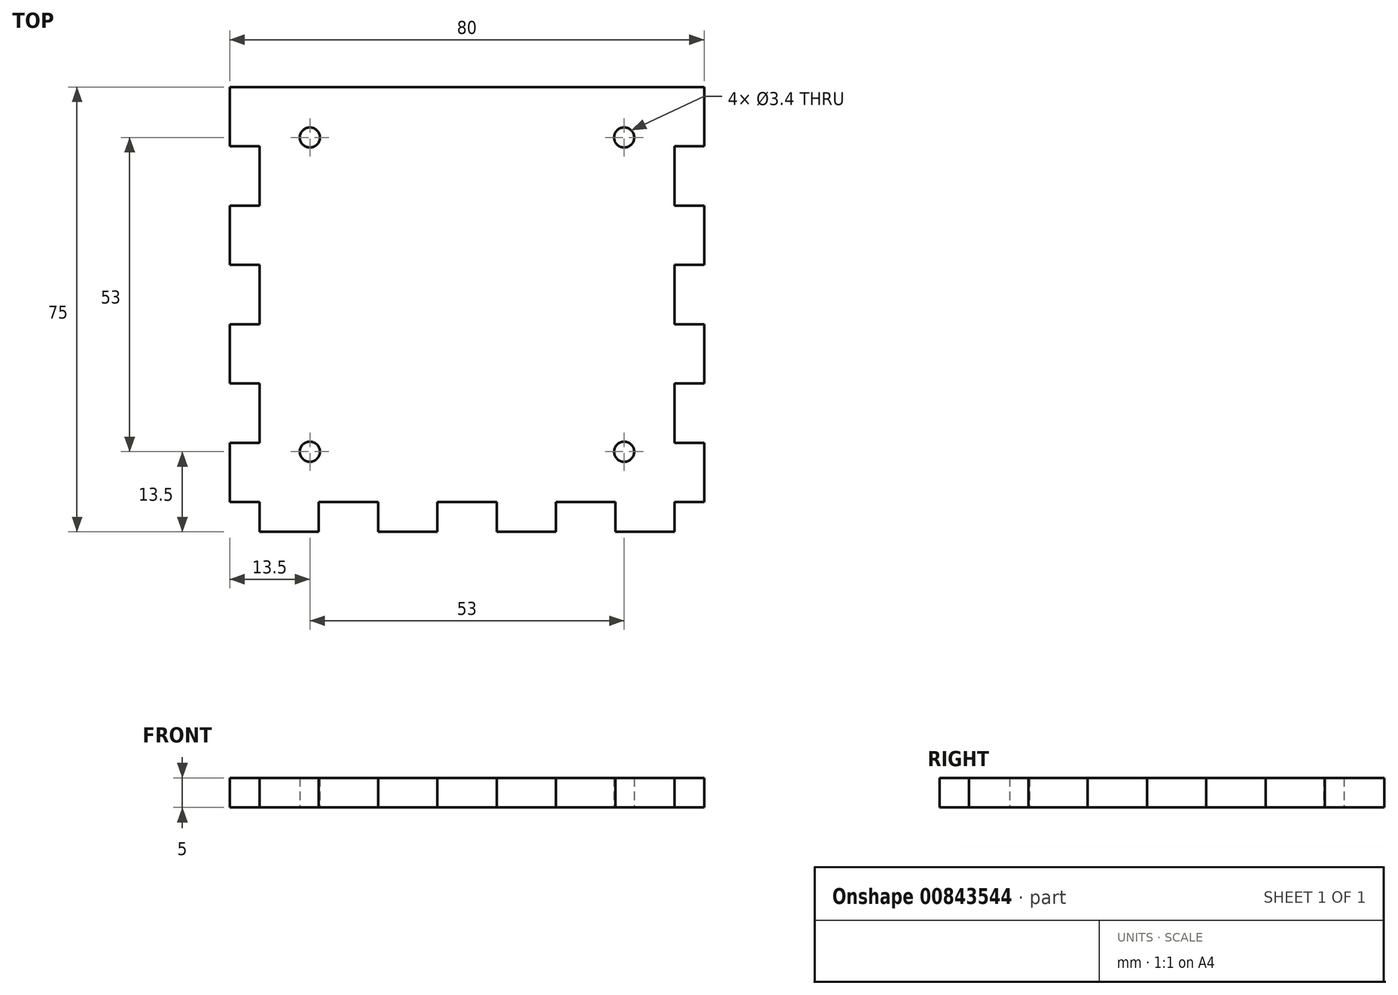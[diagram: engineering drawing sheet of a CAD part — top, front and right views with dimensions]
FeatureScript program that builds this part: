
annotation { "Feature Type Name" : "Feature", "Feature Type Description" : "" }
export const myFeature = defineFeature(function(context is Context, id is Id, definition is map)
    precondition{}
    {
        {
            var Q0;
            Q0=qCreatedBy(makeId("Top.planeOp"),FACE);
            var sketch = newSketch(context, id + "F0", { "sketchPlane" : qUnion([Q0])});
            skLineSegment(sketch, "E0.bottom", {"start": v(35, 35) * mm, "end": v(-35, 35) * mm});
            skLineSegment(sketch, "E0.top", {"start": v(35, -35) * mm, "end": v(-35, -35) * mm});
            skLineSegment(sketch, "E0.left", {"start": v(35, 35) * mm, "end": v(35, -35) * mm});
            skLineSegment(sketch, "E0.right", {"start": v(-35, 35) * mm, "end": v(-35, -35) * mm});
            skPoint(sketch, "E0.middle", {"position": v(0, 0) * mm});
            skSolve(sketch);
        }
        {
            var Q0;
            Q0=makeQuery(id+"F0.imprint","IMPRINT",FACE,{"disambiguationData":[TD([[makeQuery(id+"F0.imprint","IMPRINT",EDGE,{"derivedFrom":sQuery(id+"F0.wireOp",EDGE,"E0.bottom")}),1.0]])]});
            extrude(context, id + "F1", {"entities" : qUnion([Q0]), "endBound" : BoundingType.SYMMETRIC, "depth" : 5 * mm, "offsetDistance" : 25 * mm});
        }
        {
            var Q0;
            Q0=makeQuery(id+"F1.opExtrude","CAP_FACE",FACE,{"disambiguationData":[OSD([sQuery(id+"F0.wireOp",EDGE,"E0.bottom"),sQuery(id+"F0.wireOp",EDGE,"E0.top"),sQuery(id+"F0.wireOp",EDGE,"E0.left"),sQuery(id+"F0.wireOp",EDGE,"E0.right")])],"isStart":true});
            var sketch = newSketch(context, id + "F2", { "sketchPlane" : qUnion([Q0])});
            skLineSegment(sketch, "E1.bottom", {"start": v(-35, -35) * mm, "end": v(-40, -35) * mm});
            skLineSegment(sketch, "E1.top", {"start": v(-35, -25) * mm, "end": v(-40, -25) * mm});
            skLineSegment(sketch, "E1.left", {"start": v(-35, -35) * mm, "end": v(-35, -25) * mm});
            skLineSegment(sketch, "E1.right", {"start": v(-40, -35) * mm, "end": v(-40, -25) * mm});
            skLineSegment(sketch, "E2.bottom", {"start": v(35, -35) * mm, "end": v(40, -35) * mm});
            skLineSegment(sketch, "E2.top", {"start": v(35, -25) * mm, "end": v(40, -25) * mm});
            skLineSegment(sketch, "E2.left", {"start": v(35, -35) * mm, "end": v(35, -25) * mm});
            skLineSegment(sketch, "E2.right", {"start": v(40, -35) * mm, "end": v(40, -25) * mm});
            skLineSegment(sketch, "E3.0.1.0", {"start": v(35, -15) * mm, "end": v(40, -15) * mm});
            skLineSegment(sketch, "E3.0.1.1", {"start": v(40, -15) * mm, "end": v(40, -5) * mm});
            skLineSegment(sketch, "E3.0.1.2", {"start": v(-35, -15) * mm, "end": v(-35, -5) * mm});
            skLineSegment(sketch, "E3.0.1.3", {"start": v(-35, -15) * mm, "end": v(-40, -15) * mm});
            skLineSegment(sketch, "E3.0.1.4", {"start": v(35, -15) * mm, "end": v(35, -5) * mm});
            skLineSegment(sketch, "E3.0.1.5", {"start": v(-35, -5) * mm, "end": v(-40, -5) * mm});
            skLineSegment(sketch, "E3.0.1.6", {"start": v(35, -5) * mm, "end": v(40, -5) * mm});
            skLineSegment(sketch, "E3.0.1.7", {"start": v(-40, -15) * mm, "end": v(-40, -5) * mm});
            skLineSegment(sketch, "E3.0.2.0", {"start": v(35, 5) * mm, "end": v(40, 5) * mm});
            skLineSegment(sketch, "E3.0.2.1", {"start": v(40, 5) * mm, "end": v(40, 15) * mm});
            skLineSegment(sketch, "E3.0.2.2", {"start": v(-35, 5) * mm, "end": v(-35, 15) * mm});
            skLineSegment(sketch, "E3.0.2.3", {"start": v(-35, 5) * mm, "end": v(-40, 5) * mm});
            skLineSegment(sketch, "E3.0.2.4", {"start": v(35, 5) * mm, "end": v(35, 15) * mm});
            skLineSegment(sketch, "E3.0.2.5", {"start": v(-35, 15) * mm, "end": v(-40, 15) * mm});
            skLineSegment(sketch, "E3.0.2.6", {"start": v(35, 15) * mm, "end": v(40, 15) * mm});
            skLineSegment(sketch, "E3.0.2.7", {"start": v(-40, 5) * mm, "end": v(-40, 15) * mm});
            skLineSegment(sketch, "E3.direction1", {"start": v(-40, -35) * mm, "end": v(-15, -35) * mm, "construction": true});
            skLineSegment(sketch, "E3.direction2", {"start": v(-40, -35) * mm, "end": v(-40, -15) * mm, "construction": true});
            skLineSegment(sketch, "E4.0.0.3", {"start": v(35, 25) * mm, "end": v(40, 25) * mm});
            skLineSegment(sketch, "E4.3.0.3", {"start": v(40, 25) * mm, "end": v(40, 35) * mm});
            skLineSegment(sketch, "E4.6.0.3", {"start": v(-35, 25) * mm, "end": v(-35, 35) * mm});
            skLineSegment(sketch, "E4.9.0.3", {"start": v(-35, 25) * mm, "end": v(-40, 25) * mm});
            skLineSegment(sketch, "E4.12.0.3", {"start": v(35, 25) * mm, "end": v(35, 35) * mm});
            skLineSegment(sketch, "E4.15.0.3", {"start": v(-35, 35) * mm, "end": v(-40, 35) * mm});
            skLineSegment(sketch, "E4.18.0.3", {"start": v(35, 35) * mm, "end": v(40, 35) * mm});
            skLineSegment(sketch, "E4.21.0.3", {"start": v(-40, 25) * mm, "end": v(-40, 35) * mm});
            skSolve(sketch);
        }
        {
            var Q0;
            Q0 = qSketchRegion(id + "F2", true);
            var Q1;
            Q1=makeQuery(id+"F1.opExtrude","CAP_FACE",FACE,{"disambiguationData":[OSD([sQuery(id+"F0.wireOp",EDGE,"E0.bottom"),sQuery(id+"F0.wireOp",EDGE,"E0.top"),sQuery(id+"F0.wireOp",EDGE,"E0.left"),sQuery(id+"F0.wireOp",EDGE,"E0.right")])],"isStart":false});
            extrude(context, id + "F3", {"entities" : qUnion([Q0]), "operationType" : NewBodyOperationType.ADD, "endBound" : BoundingType.UP_TO_SURFACE, "oppositeDirection" : true, "depth" : 25 * mm, "endBoundEntityFace" : qUnion([Q1]), "offsetDistance" : 25 * mm});
        }
        {
            var Q0;
            Q0=makeQuery(id+"F3.boolean.opBoolean","MERGE",FACE,{"derivedFrom":[makeQuery(id+"F1.opExtrude","CAP_FACE",FACE,{"disambiguationData":[OSD([sQuery(id+"F0.wireOp",EDGE,"E0.bottom"),sQuery(id+"F0.wireOp",EDGE,"E0.top"),sQuery(id+"F0.wireOp",EDGE,"E0.left"),sQuery(id+"F0.wireOp",EDGE,"E0.right")])],"isStart":true}),makeQuery(id+"F3.opExtrude","CAP_FACE",FACE,{"disambiguationData":[OSD([sQuery(id+"F2.wireOp",EDGE,"E1.bottom"),sQuery(id+"F2.wireOp",EDGE,"E1.top"),sQuery(id+"F2.wireOp",EDGE,"E1.left"),sQuery(id+"F2.wireOp",EDGE,"E1.right")])],"isStart":true}),makeQuery(id+"F3.opExtrude","CAP_FACE",FACE,{"disambiguationData":[OSD([sQuery(id+"F2.wireOp",EDGE,"E2.bottom"),sQuery(id+"F2.wireOp",EDGE,"E2.top"),sQuery(id+"F2.wireOp",EDGE,"E2.left"),sQuery(id+"F2.wireOp",EDGE,"E2.right")])],"isStart":true}),makeQuery(id+"F3.opExtrude","CAP_FACE",FACE,{"disambiguationData":[OSD([sQuery(id+"F2.wireOp",EDGE,"E3.0.1.0"),sQuery(id+"F2.wireOp",EDGE,"E3.0.1.1"),sQuery(id+"F2.wireOp",EDGE,"E3.0.1.4"),sQuery(id+"F2.wireOp",EDGE,"E3.0.1.6")])],"isStart":true}),makeQuery(id+"F3.opExtrude","CAP_FACE",FACE,{"disambiguationData":[OSD([sQuery(id+"F2.wireOp",EDGE,"E3.0.1.2"),sQuery(id+"F2.wireOp",EDGE,"E3.0.1.3"),sQuery(id+"F2.wireOp",EDGE,"E3.0.1.5"),sQuery(id+"F2.wireOp",EDGE,"E3.0.1.7")])],"isStart":true}),makeQuery(id+"F3.opExtrude","CAP_FACE",FACE,{"disambiguationData":[OSD([sQuery(id+"F2.wireOp",EDGE,"E3.0.2.0"),sQuery(id+"F2.wireOp",EDGE,"E3.0.2.1"),sQuery(id+"F2.wireOp",EDGE,"E3.0.2.4"),sQuery(id+"F2.wireOp",EDGE,"E3.0.2.6")])],"isStart":true}),makeQuery(id+"F3.opExtrude","CAP_FACE",FACE,{"disambiguationData":[OSD([sQuery(id+"F2.wireOp",EDGE,"E3.0.2.2"),sQuery(id+"F2.wireOp",EDGE,"E3.0.2.3"),sQuery(id+"F2.wireOp",EDGE,"E3.0.2.5"),sQuery(id+"F2.wireOp",EDGE,"E3.0.2.7")])],"isStart":true}),makeQuery(id+"F3.opExtrude","CAP_FACE",FACE,{"disambiguationData":[OSD([sQuery(id+"F2.wireOp",EDGE,"E4.0.0.3"),sQuery(id+"F2.wireOp",EDGE,"E4.3.0.3"),sQuery(id+"F2.wireOp",EDGE,"E4.12.0.3"),sQuery(id+"F2.wireOp",EDGE,"E4.18.0.3")])],"isStart":true}),makeQuery(id+"F3.opExtrude","CAP_FACE",FACE,{"disambiguationData":[OSD([sQuery(id+"F2.wireOp",EDGE,"E4.6.0.3"),sQuery(id+"F2.wireOp",EDGE,"E4.9.0.3"),sQuery(id+"F2.wireOp",EDGE,"E4.15.0.3"),sQuery(id+"F2.wireOp",EDGE,"E4.21.0.3")])],"isStart":true})]});
            var sketch = newSketch(context, id + "F4", { "sketchPlane" : qUnion([Q0])});
            skLineSegment(sketch, "E5.bottom", {"start": v(-35, 35) * mm, "end": v(-25, 35) * mm});
            skLineSegment(sketch, "E5.top", {"start": v(-35, 40) * mm, "end": v(-25, 40) * mm});
            skLineSegment(sketch, "E5.left", {"start": v(-35, 35) * mm, "end": v(-35, 40) * mm});
            skLineSegment(sketch, "E5.right", {"start": v(-25, 35) * mm, "end": v(-25, 40) * mm});
            skLineSegment(sketch, "E6.1.0.0", {"start": v(-5, 35) * mm, "end": v(-5, 40) * mm});
            skLineSegment(sketch, "E6.1.0.1", {"start": v(-15, 40) * mm, "end": v(-5, 40) * mm});
            skLineSegment(sketch, "E6.1.0.2", {"start": v(-15, 35) * mm, "end": v(-15, 40) * mm});
            skLineSegment(sketch, "E6.1.0.3", {"start": v(-15, 35) * mm, "end": v(-5, 35) * mm});
            skLineSegment(sketch, "E6.2.0.0", {"start": v(15, 35) * mm, "end": v(15, 40) * mm});
            skLineSegment(sketch, "E6.2.0.1", {"start": v(5, 40) * mm, "end": v(15, 40) * mm});
            skLineSegment(sketch, "E6.2.0.2", {"start": v(5, 35) * mm, "end": v(5, 40) * mm});
            skLineSegment(sketch, "E6.2.0.3", {"start": v(5, 35) * mm, "end": v(15, 35) * mm});
            skLineSegment(sketch, "E6.3.0.0", {"start": v(35, 35) * mm, "end": v(35, 40) * mm});
            skLineSegment(sketch, "E6.3.0.1", {"start": v(25, 40) * mm, "end": v(35, 40) * mm});
            skLineSegment(sketch, "E6.3.0.2", {"start": v(25, 35) * mm, "end": v(25, 40) * mm});
            skLineSegment(sketch, "E6.3.0.3", {"start": v(25, 35) * mm, "end": v(35, 35) * mm});
            skLineSegment(sketch, "E6.direction1", {"start": v(-35, 35) * mm, "end": v(-15, 35) * mm, "construction": true});
            skSolve(sketch);
        }
        {
            var Q0;
            Q0 = qSketchRegion(id + "F4", true);
            var Q1;
            {var subQ0=sQuery(id+"F0.wireOp",EDGE,"E0.right");var subQ1=sQuery(id+"F0.wireOp",EDGE,"E0.left");var subQ2=sQuery(id+"F0.wireOp",EDGE,"E0.top");var subQ3=sQuery(id+"F0.wireOp",EDGE,"E0.bottom");Q1=makeQuery(id+"F3.boolean.opBoolean","MERGE",FACE,{"derivedFrom":[makeQuery(id+"F1.opExtrude","CAP_FACE",FACE,{"disambiguationData":[OSD([subQ3,subQ2,subQ1,subQ0])],"isStart":false}),makeQuery(id+"F3.opExtrude","CAP_FACE",FACE,{"disambiguationData":[OSD([subQ3,subQ2,subQ1,subQ0]),OD(0.0)],"isStart":false}),makeQuery(id+"F3.opExtrude","CAP_FACE",FACE,{"disambiguationData":[OSD([subQ3,subQ2,subQ1,subQ0]),OD(1.0)],"isStart":false}),makeQuery(id+"F3.opExtrude","CAP_FACE",FACE,{"disambiguationData":[OSD([subQ3,subQ2,subQ1,subQ0]),OD(2.0)],"isStart":false}),makeQuery(id+"F3.opExtrude","CAP_FACE",FACE,{"disambiguationData":[OSD([subQ3,subQ2,subQ1,subQ0]),OD(3.0)],"isStart":false}),makeQuery(id+"F3.opExtrude","CAP_FACE",FACE,{"disambiguationData":[OSD([subQ3,subQ2,subQ1,subQ0]),OD(4.0)],"isStart":false}),makeQuery(id+"F3.opExtrude","CAP_FACE",FACE,{"disambiguationData":[OSD([subQ3,subQ2,subQ1,subQ0]),OD(5.0)],"isStart":false}),makeQuery(id+"F3.opExtrude","CAP_FACE",FACE,{"disambiguationData":[OSD([subQ3,subQ2,subQ1,subQ0]),OD(6.0)],"isStart":false}),makeQuery(id+"F3.opExtrude","CAP_FACE",FACE,{"disambiguationData":[OSD([subQ3,subQ2,subQ1,subQ0]),OD(7.0)],"isStart":false})]});}
            extrude(context, id + "F5", {"entities" : qUnion([Q0]), "operationType" : NewBodyOperationType.ADD, "endBound" : BoundingType.UP_TO_SURFACE, "oppositeDirection" : true, "depth" : 25 * mm, "endBoundEntityFace" : qUnion([Q1]), "offsetDistance" : 25 * mm});
        }
        {
            var Q0;
            Q0=makeQuery(id+"F5.boolean.opBoolean","MERGE",FACE,{"derivedFrom":[makeQuery(id+"F3.boolean.opBoolean","MERGE",FACE,{"derivedFrom":[makeQuery(id+"F1.opExtrude","CAP_FACE",FACE,{"disambiguationData":[OSD([sQuery(id+"F0.wireOp",EDGE,"E0.bottom"),sQuery(id+"F0.wireOp",EDGE,"E0.top"),sQuery(id+"F0.wireOp",EDGE,"E0.left"),sQuery(id+"F0.wireOp",EDGE,"E0.right")])],"isStart":true}),makeQuery(id+"F3.opExtrude","CAP_FACE",FACE,{"disambiguationData":[OSD([sQuery(id+"F2.wireOp",EDGE,"E1.bottom"),sQuery(id+"F2.wireOp",EDGE,"E1.top"),sQuery(id+"F2.wireOp",EDGE,"E1.left"),sQuery(id+"F2.wireOp",EDGE,"E1.right")])],"isStart":true}),makeQuery(id+"F3.opExtrude","CAP_FACE",FACE,{"disambiguationData":[OSD([sQuery(id+"F2.wireOp",EDGE,"E2.bottom"),sQuery(id+"F2.wireOp",EDGE,"E2.top"),sQuery(id+"F2.wireOp",EDGE,"E2.left"),sQuery(id+"F2.wireOp",EDGE,"E2.right")])],"isStart":true}),makeQuery(id+"F3.opExtrude","CAP_FACE",FACE,{"disambiguationData":[OSD([sQuery(id+"F2.wireOp",EDGE,"E3.0.1.0"),sQuery(id+"F2.wireOp",EDGE,"E3.0.1.1"),sQuery(id+"F2.wireOp",EDGE,"E3.0.1.4"),sQuery(id+"F2.wireOp",EDGE,"E3.0.1.6")])],"isStart":true}),makeQuery(id+"F3.opExtrude","CAP_FACE",FACE,{"disambiguationData":[OSD([sQuery(id+"F2.wireOp",EDGE,"E3.0.1.2"),sQuery(id+"F2.wireOp",EDGE,"E3.0.1.3"),sQuery(id+"F2.wireOp",EDGE,"E3.0.1.5"),sQuery(id+"F2.wireOp",EDGE,"E3.0.1.7")])],"isStart":true}),makeQuery(id+"F3.opExtrude","CAP_FACE",FACE,{"disambiguationData":[OSD([sQuery(id+"F2.wireOp",EDGE,"E3.0.2.0"),sQuery(id+"F2.wireOp",EDGE,"E3.0.2.1"),sQuery(id+"F2.wireOp",EDGE,"E3.0.2.4"),sQuery(id+"F2.wireOp",EDGE,"E3.0.2.6")])],"isStart":true}),makeQuery(id+"F3.opExtrude","CAP_FACE",FACE,{"disambiguationData":[OSD([sQuery(id+"F2.wireOp",EDGE,"E3.0.2.2"),sQuery(id+"F2.wireOp",EDGE,"E3.0.2.3"),sQuery(id+"F2.wireOp",EDGE,"E3.0.2.5"),sQuery(id+"F2.wireOp",EDGE,"E3.0.2.7")])],"isStart":true}),makeQuery(id+"F3.opExtrude","CAP_FACE",FACE,{"disambiguationData":[OSD([sQuery(id+"F2.wireOp",EDGE,"E4.0.0.3"),sQuery(id+"F2.wireOp",EDGE,"E4.3.0.3"),sQuery(id+"F2.wireOp",EDGE,"E4.12.0.3"),sQuery(id+"F2.wireOp",EDGE,"E4.18.0.3")])],"isStart":true}),makeQuery(id+"F3.opExtrude","CAP_FACE",FACE,{"disambiguationData":[OSD([sQuery(id+"F2.wireOp",EDGE,"E4.6.0.3"),sQuery(id+"F2.wireOp",EDGE,"E4.9.0.3"),sQuery(id+"F2.wireOp",EDGE,"E4.15.0.3"),sQuery(id+"F2.wireOp",EDGE,"E4.21.0.3")])],"isStart":true})]}),makeQuery(id+"F5.opExtrude","CAP_FACE",FACE,{"disambiguationData":[OSD([sQuery(id+"F4.wireOp",EDGE,"E5.bottom"),sQuery(id+"F4.wireOp",EDGE,"E5.top"),sQuery(id+"F4.wireOp",EDGE,"E5.left"),sQuery(id+"F4.wireOp",EDGE,"E5.right")])],"isStart":true}),makeQuery(id+"F5.opExtrude","CAP_FACE",FACE,{"disambiguationData":[OSD([sQuery(id+"F4.wireOp",EDGE,"E6.1.0.0"),sQuery(id+"F4.wireOp",EDGE,"E6.1.0.1"),sQuery(id+"F4.wireOp",EDGE,"E6.1.0.2"),sQuery(id+"F4.wireOp",EDGE,"E6.1.0.3")])],"isStart":true}),makeQuery(id+"F5.opExtrude","CAP_FACE",FACE,{"disambiguationData":[OSD([sQuery(id+"F4.wireOp",EDGE,"E6.2.0.0"),sQuery(id+"F4.wireOp",EDGE,"E6.2.0.1"),sQuery(id+"F4.wireOp",EDGE,"E6.2.0.2"),sQuery(id+"F4.wireOp",EDGE,"E6.2.0.3")])],"isStart":true}),makeQuery(id+"F5.opExtrude","CAP_FACE",FACE,{"disambiguationData":[OSD([sQuery(id+"F4.wireOp",EDGE,"E6.3.0.0"),sQuery(id+"F4.wireOp",EDGE,"E6.3.0.1"),sQuery(id+"F4.wireOp",EDGE,"E6.3.0.2"),sQuery(id+"F4.wireOp",EDGE,"E6.3.0.3")])],"isStart":true})]});
            var sketch = newSketch(context, id + "F6", { "sketchPlane" : qUnion([Q0])});
            skLineSegment(sketch, "E7.bottom", {"start": v(-26.5, -26.5) * mm, "end": v(26.5, -26.5) * mm, "construction": true});
            skLineSegment(sketch, "E7.top", {"start": v(-26.5, 26.5) * mm, "end": v(26.5, 26.5) * mm, "construction": true});
            skLineSegment(sketch, "E7.left", {"start": v(-26.5, -26.5) * mm, "end": v(-26.5, 26.5) * mm, "construction": true});
            skLineSegment(sketch, "E7.right", {"start": v(26.5, -26.5) * mm, "end": v(26.5, 26.5) * mm, "construction": true});
            skLineSegment(sketch, "E8", {"start": v(26.5, 26.5) * mm, "end": v(-26.5, -26.5) * mm, "construction": true});
            skLineSegment(sketch, "E9.direction2", {"start": v(-26.5, 26.5) * mm, "end": v(-26.5, -26.5) * mm, "construction": true});
            skSolve(sketch);
        }
        {
            var Q0;
            Q0=sQuery(id+"F6.wireOp",VERTEX,"E7.top.start");
            var Q1;
            Q1=sQuery(id+"F6.wireOp",VERTEX,"E7.top.end");
            var Q2;
            Q2=sQuery(id+"F6.wireOp",VERTEX,"E7.bottom.end");
            var Q3;
            Q3=sQuery(id+"F6.wireOp",VERTEX,"E7.bottom.start");
            var Q4;
            Q4=makeQuery(id+"F1.opExtrude","SWEPT_BODY",BODY,{"disambiguationData":[OSD([sQuery(id+"F0.wireOp",EDGE,"E0.bottom"),sQuery(id+"F0.wireOp",EDGE,"E0.top"),sQuery(id+"F0.wireOp",EDGE,"E0.left"),sQuery(id+"F0.wireOp",EDGE,"E0.right")])]});
            hole(context, id + "F7", {"style" : HoleStyle.SIMPLE, "endStyle" : HoleEndStyle.THROUGH, "holeDiameter" : 3.4 * mm, "majorDiameter" : 5 * mm, "isTappedThrough" : true, "tappedDepth" : 12 * mm, "tapClearance" : 3, "locations" : qUnion([Q0, Q1, Q2, Q3]), "scope" : qUnion([Q4])});
        }
    });
